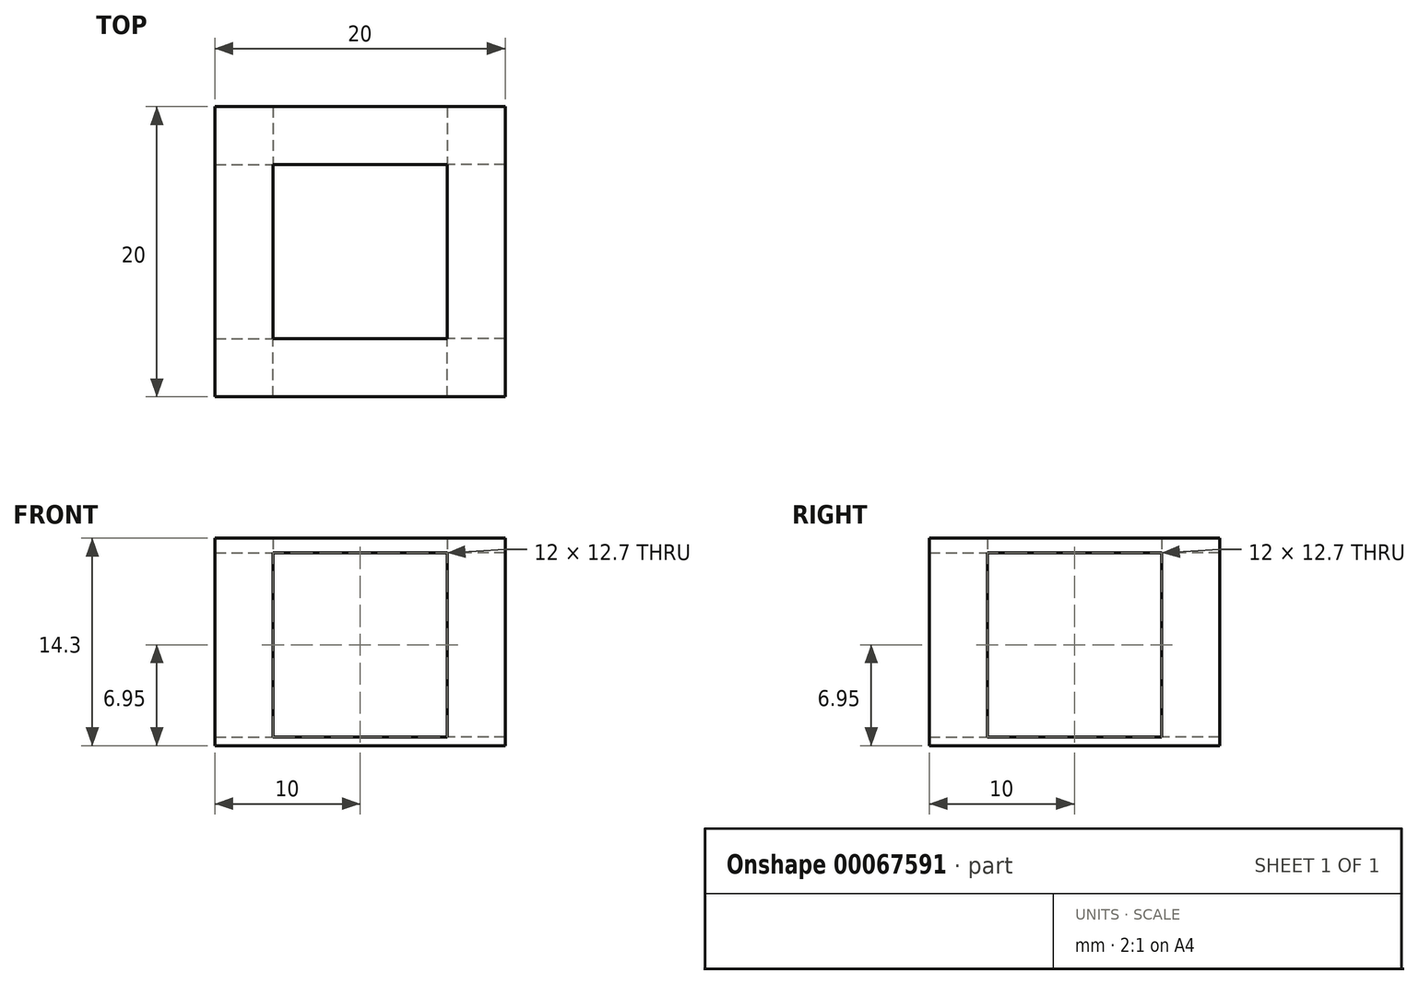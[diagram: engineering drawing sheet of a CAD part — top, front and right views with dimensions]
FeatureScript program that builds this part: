
annotation { "Feature Type Name" : "Feature", "Feature Type Description" : "" }
export const myFeature = defineFeature(function(context is Context, id is Id, definition is map)
    precondition{}
    {
        {
            var Q0;
            Q0=qCreatedBy(makeId("Top.planeOp"),FACE);
            var sketch = newSketch(context, id + "F0", { "sketchPlane" : qUnion([Q0])});
            skLineSegment(sketch, "E0.rect.bottom", {"start": v(10, 10) * mm, "end": v(-10, 10) * mm});
            skLineSegment(sketch, "E0.rect.top", {"start": v(10, -10) * mm, "end": v(-10, -10) * mm});
            skLineSegment(sketch, "E0.rect.left", {"start": v(10, 10) * mm, "end": v(10, -10) * mm});
            skLineSegment(sketch, "E0.rect.right", {"start": v(-10, 10) * mm, "end": v(-10, -10) * mm});
            skPoint(sketch, "E0.rect.middle", {"position": v(0, 0) * mm});
            skSolve(sketch);
        }
        {
            var Q0;
            Q0 = qSketchRegion(id + "F0", true);
            extrude(context, id + "F1", {"entities" : qUnion([Q0]), "depth" : .6 * mm});
        }
        {
            var Q0;
            Q0=makeQuery(id+"F1.opExtrude","CAP_FACE",FACE,{"disambiguationData":[OSD([sQuery(id+"F0.wireOp",EDGE,"E0.rect.bottom"),sQuery(id+"F0.wireOp",EDGE,"E0.rect.top"),sQuery(id+"F0.wireOp",EDGE,"E0.rect.left"),sQuery(id+"F0.wireOp",EDGE,"E0.rect.right")])],"isStart":false});
            var sketch = newSketch(context, id + "F2", { "sketchPlane" : qUnion([Q0])});
            skLineSegment(sketch, "E1.bottom", {"start": v(-10, 10) * mm, "end": v(-6, 10) * mm});
            skLineSegment(sketch, "E1.top", {"start": v(-10, 6) * mm, "end": v(-6, 6) * mm});
            skLineSegment(sketch, "E1.left", {"start": v(-10, 10) * mm, "end": v(-10, 6) * mm});
            skLineSegment(sketch, "E1.right", {"start": v(-6, 10) * mm, "end": v(-6, 6) * mm});
            skSolve(sketch);
        }
        {
            var Q0;
            Q0 = qSketchRegion(id + "F2", true);
            extrude(context, id + "F3", {"entities" : qUnion([Q0]), "operationType" : NewBodyOperationType.ADD, "depth" : 12.7 * mm});
        }
        {
            var Q0;
            Q0=makeQuery(id+"F1.opExtrude","SWEPT_BODY",BODY,{"disambiguationData":[OSD([sQuery(id+"F0.wireOp",EDGE,"E0.rect.bottom"),sQuery(id+"F0.wireOp",EDGE,"E0.rect.top"),sQuery(id+"F0.wireOp",EDGE,"E0.rect.left"),sQuery(id+"F0.wireOp",EDGE,"E0.rect.right")])]});
            var Q1;
            Q1=qCreatedBy(makeId("Right.planeOp"),FACE);
            mirror(context, id + "F4", {"operationType" : NewBodyOperationType.ADD, "entities" : qUnion([Q0]), "mirrorPlane" : qUnion([Q1])});
        }
        {
            var Q0;
            Q0=makeQuery(id+"F1.opExtrude","SWEPT_BODY",BODY,{"disambiguationData":[OSD([sQuery(id+"F0.wireOp",EDGE,"E0.rect.bottom"),sQuery(id+"F0.wireOp",EDGE,"E0.rect.top"),sQuery(id+"F0.wireOp",EDGE,"E0.rect.left"),sQuery(id+"F0.wireOp",EDGE,"E0.rect.right")])]});
            var Q1;
            Q1=qCreatedBy(makeId("Front.planeOp"),FACE);
            mirror(context, id + "F5", {"operationType" : NewBodyOperationType.ADD, "entities" : qUnion([Q0]), "mirrorPlane" : qUnion([Q1])});
        }
        {
            var Q0;
            Q0=makeQuery(id+"F3.opExtrude","CAP_FACE",FACE,{"disambiguationData":[OSD([sQuery(id+"F2.wireOp",EDGE,"E1.bottom"),sQuery(id+"F2.wireOp",EDGE,"E1.top"),sQuery(id+"F2.wireOp",EDGE,"E1.left"),sQuery(id+"F2.wireOp",EDGE,"E1.right")])],"isStart":false});
            var sketch = newSketch(context, id + "F6", { "sketchPlane" : qUnion([Q0])});
            skLineSegment(sketch, "E2.0.0", {"start": v(10, 10) * mm, "end": v(10, -10) * mm});
            skLineSegment(sketch, "E2.0.1", {"start": v(10, -10) * mm, "end": v(-10, -10) * mm});
            skLineSegment(sketch, "E2.0.2", {"start": v(-10, -10) * mm, "end": v(-10, 10) * mm});
            skLineSegment(sketch, "E2.0.3", {"start": v(-10, 10) * mm, "end": v(10, 10) * mm});
            skLineSegment(sketch, "E3.bottom", {"start": v(6, 6) * mm, "end": v(-6, 6) * mm});
            skLineSegment(sketch, "E3.top", {"start": v(6, -6) * mm, "end": v(-6, -6) * mm});
            skLineSegment(sketch, "E3.left", {"start": v(6, 6) * mm, "end": v(6, -6) * mm});
            skLineSegment(sketch, "E3.right", {"start": v(-6, 6) * mm, "end": v(-6, -6) * mm});
            skSolve(sketch);
        }
        {
            var Q0;
            Q0 = qSketchRegion(id + "F6", true);
            extrude(context, id + "F7", {"entities" : qUnion([Q0]), "operationType" : NewBodyOperationType.ADD, "depth" : 1 * mm});
        }
    });
